# Revit family: ledpanelsp-z_l1222-75w-dali-4000-al_140054054
name_source: partatom
category: Leuchten
revit_build: Autodesk Revit 2016 (Build: 20190508_0715(x64)
units: mm (PartAtom-declared; Revit-internal decimal feet)

## family parameters
Basisbauteil = Fläche
Beim Laden mit Abzugskörper schneiden = Nein
Bemaßung runder Anschluss = Durchmesser verwenden
Gemeinsam genutzt = Nein
Lichtquelle = Nein
Raumberechnungspunkt = Nein
Teiletyp = Normal

## types (1)
- LEDPanelSp-Z L1222-75W-DALI-4000-AL (1 x LED, 7500 lm)
    Approval mark = CE, ENEC
    Beschreibung = Special design luminaire distributes light both up and down, combining comfort and efficiency. Light up your offices and meeting rooms in an architectural way. Save up to 50% energy compared to fluorescent solutions. Standard including suspension kit (2.5m) and separate aluminum colored driver housing.
    CIE Flux Codes = 46 77 94 48 100
    Control Gear = Electronic ballast
    Height = 187 mm
    Hersteller = OPPLE
    Lamp Light Flux = 7500 lm
    Lamp count = 1
    Lampe = 1 x LED
    Length = 1222 mm
    Luminous efficacy = 100 lm/W
    ModVariant = Nein
    Modell = 140054054
    Mounting Place = Ceiling
    Mounting Type = Pendant
    Number of Poles = 1
    OnlyDefault = Ja
    Power Factor = 1
    Product Name = LEDPanelSp-Z L1222-75W-DALI-4000-AL
    Product group = Panel Suspended Zenith
    ProductGroupID = 920
    Protection Class = Protection class II
    Protection Degree = IP 20
    RLX_Detail_Level = 1
    RlxData = <blob elided: 95605 chars, md5=d938122a>
    Scheinlast = 75 VA
    Socket = socket
    Standby Power = 0 W
    System Light Flux = 7500 lm
    System Power = 75 W
    Typenbild = 140054054.jpg
    Typenkommentare = Product without accessories
    URL = http://relux.com
    VarID = ---
    Voltage = 0 V
    Vorgabe-Ansicht = 1800 mm
    Weight = 0.00 kg
    Width = 2355 mm

## geometry (parser evidence)
native form markers: Blend x4, Sweep x17
no freeform markers — native parametric forms only
